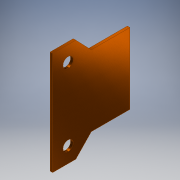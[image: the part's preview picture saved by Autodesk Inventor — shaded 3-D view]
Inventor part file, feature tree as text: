
AUTODESK INVENTOR PART (.ipt)
format: ipt  version: 2018.2 (Build 222227000, 227)  size: 139,776 bytes
history: native  units: mm
features: other x1, extrude x1, sketch x1
ambient origin geometry x8: Origin, YZ Plane, XZ Plane, XY Plane, X Axis, Y Axis, Z Axis, Center Point
bodies: Body1 (feature_tree)
feature tree (3):
  other  "Твердое тело1"
  extrude  "Выдавливание1"  Depth=40.0mm
  sketch  "Эскиз1"
